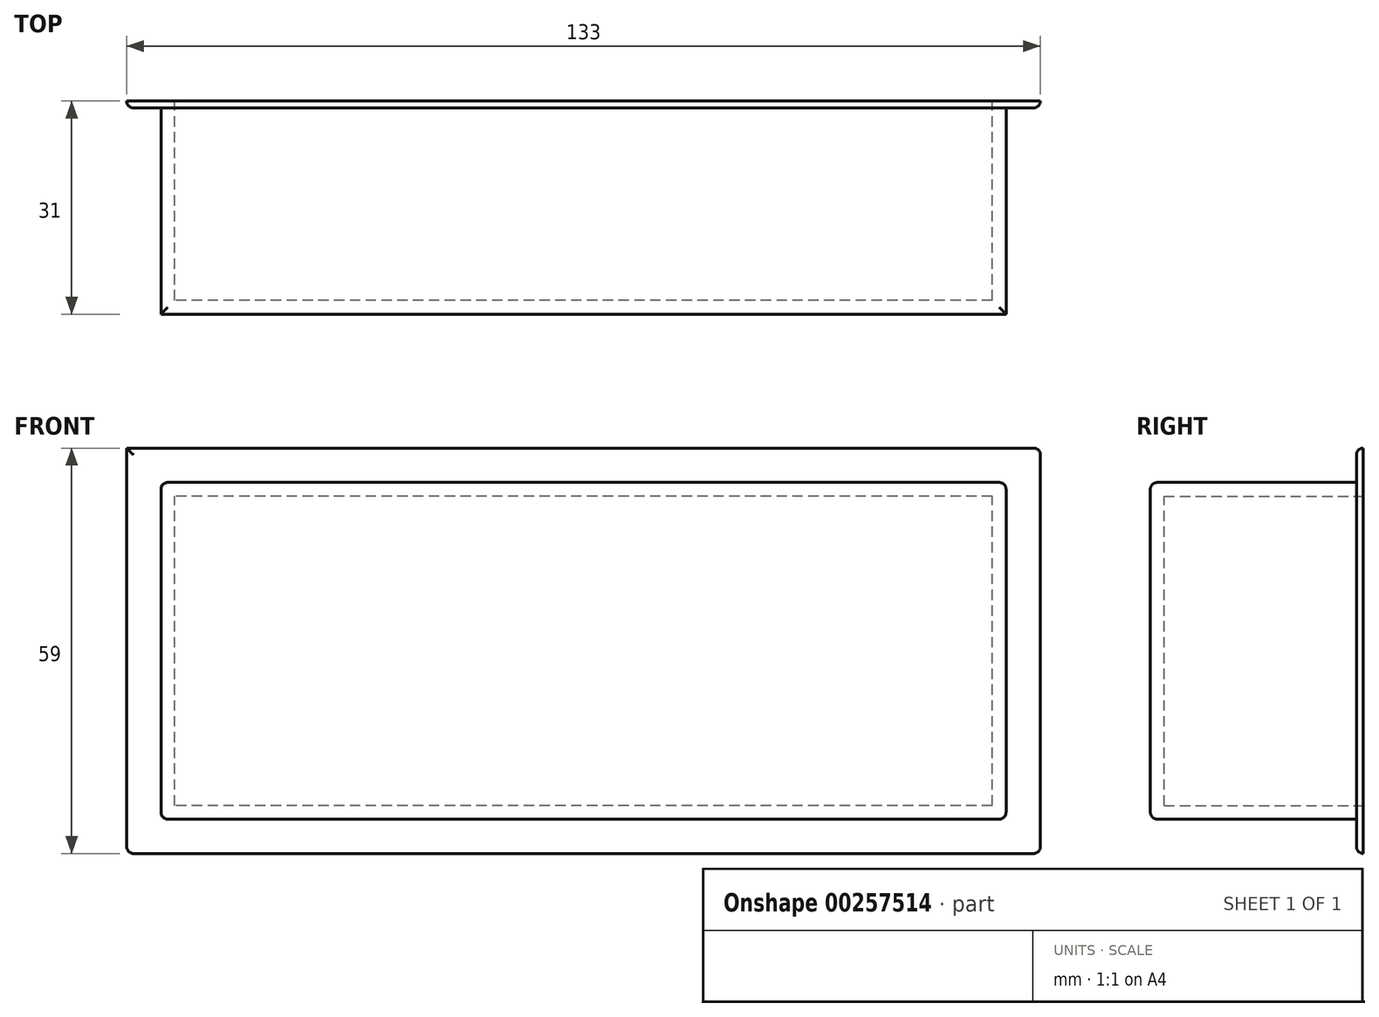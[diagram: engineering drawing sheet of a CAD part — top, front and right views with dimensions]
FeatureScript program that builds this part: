
annotation { "Feature Type Name" : "Feature", "Feature Type Description" : "" }
export const myFeature = defineFeature(function(context is Context, id is Id, definition is map)
    precondition{}
    {
        {
            var Q0;
            Q0=qCreatedBy(makeId("Front.planeOp"),FACE);
            cPlane(context, id + "F0", {"entities" : qUnion([Q0]), "cplaneType" : CPlaneType.OFFSET, "offset" : 15 * mm, "width" : 150 * mm, "height" : 150 * mm});
        }
        {
            var Q0;
            Q0=qCreatedBy(id+"F0.planeOp",FACE);
            var sketch = newSketch(context, id + "F1", { "sketchPlane" : qUnion([Q0])});
            skLineSegment(sketch, "E0.bottom", {"start": v(61.5, -24.5) * mm, "end": v(-61.5, -24.5) * mm});
            skLineSegment(sketch, "E0.top", {"start": v(61.5, 24.5) * mm, "end": v(-61.5, 24.5) * mm});
            skLineSegment(sketch, "E0.left", {"start": v(61.5, -24.5) * mm, "end": v(61.5, 24.5) * mm});
            skLineSegment(sketch, "E0.right", {"start": v(-61.5, -24.5) * mm, "end": v(-61.5, 24.5) * mm});
            skPoint(sketch, "E0.middle", {"position": v(0, 0) * mm});
            skLineSegment(sketch, "E1.bottom", {"start": v(59.5, -22.5) * mm, "end": v(-59.5, -22.5) * mm});
            skLineSegment(sketch, "E1.top", {"start": v(59.5, 22.5) * mm, "end": v(-59.5, 22.5) * mm});
            skLineSegment(sketch, "E1.left", {"start": v(59.5, -22.5) * mm, "end": v(59.5, 22.5) * mm});
            skLineSegment(sketch, "E1.right", {"start": v(-59.5, -22.5) * mm, "end": v(-59.5, 22.5) * mm});
            skLineSegment(sketch, "E2.top", {"start": v(61.5, 29.5) * mm, "end": v(-61.5, 29.5) * mm});
            skLineSegment(sketch, "E2.left", {"start": v(61.5, 24.5) * mm, "end": v(61.5, 29.5) * mm});
            skLineSegment(sketch, "E2.right", {"start": v(-61.5, 24.5) * mm, "end": v(-61.5, 29.5) * mm});
            skLineSegment(sketch, "E3.top", {"start": v(61.5, -29.5) * mm, "end": v(-61.5, -29.5) * mm});
            skLineSegment(sketch, "E3.left", {"start": v(61.5, -24.5) * mm, "end": v(61.5, -29.5) * mm});
            skLineSegment(sketch, "E3.right", {"start": v(-61.5, -24.5) * mm, "end": v(-61.5, -29.5) * mm});
            skLineSegment(sketch, "E4.bottom", {"start": v(-61.5, 29.5) * mm, "end": v(-66.5, 29.5) * mm});
            skLineSegment(sketch, "E4.top", {"start": v(-61.5, -29.5) * mm, "end": v(-66.5, -29.5) * mm});
            skLineSegment(sketch, "E4.left", {"start": v(-61.5, 29.5) * mm, "end": v(-61.5, -29.5) * mm});
            skLineSegment(sketch, "E4.right", {"start": v(-66.5, 29.5) * mm, "end": v(-66.5, -29.5) * mm});
            skLineSegment(sketch, "E5.bottom", {"start": v(61.5, 29.5) * mm, "end": v(66.5, 29.5) * mm});
            skLineSegment(sketch, "E5.top", {"start": v(61.5, -29.5) * mm, "end": v(66.5, -29.5) * mm});
            skLineSegment(sketch, "E5.left", {"start": v(61.5, 29.5) * mm, "end": v(61.5, -29.5) * mm});
            skLineSegment(sketch, "E5.right", {"start": v(66.5, 29.5) * mm, "end": v(66.5, -29.5) * mm});
            skSolve(sketch);
        }
        {
            var Q0;
            Q0=makeQuery(id+"F1.imprint","IMPRINT",FACE,{"disambiguationData":[TD([[makeQuery(id+"F1.imprint","IMPRINT",EDGE,{"derivedFrom":sQuery(id+"F1.wireOp",EDGE,"E1.bottom")}),1.0]])]});
            extrude(context, id + "F2", {"entities" : qUnion([Q0]), "depth" : 31 * mm});
        }
        {
            var Q0;
            {var subQ0=sQuery(id+"F1.wireOp",EDGE,"E0.top");Q0=makeQuery(id+"F1.imprint","IMPRINT",FACE,{"disambiguationData":[TD([[makeQuery(id+"F1.imprint","IMPRINT",EDGE,{"derivedFrom":subQ0}),-1.0]])]});}
            var Q1;
            {var subQ4=sQuery(id+"F1.wireOp",EDGE,"E4.bottom");Q1=makeQuery(id+"F1.imprint","IMPRINT",FACE,{"disambiguationData":[TD([[makeQuery(id+"F1.imprint","IMPRINT",EDGE,{"derivedFrom":subQ4}),1.0]])]});}
            var Q2;
            {var subQ0=sQuery(id+"F1.wireOp",EDGE,"E0.bottom");Q2=makeQuery(id+"F1.imprint","IMPRINT",FACE,{"disambiguationData":[TD([[makeQuery(id+"F1.imprint","IMPRINT",EDGE,{"derivedFrom":subQ0}),1.0]])]});}
            var Q3;
            {var subQ3=sQuery(id+"F1.wireOp",EDGE,"E5.bottom");Q3=makeQuery(id+"F1.imprint","IMPRINT",FACE,{"disambiguationData":[TD([[makeQuery(id+"F1.imprint","IMPRINT",EDGE,{"derivedFrom":subQ3}),-1.0]])]});}
            extrude(context, id + "F3", {"entities" : qUnion([Q0, Q1, Q2, Q3]), "operationType" : NewBodyOperationType.ADD, "depth" : 1 * mm});
        }
        {
            var Q0;
            Q0=makeQuery(id+"F1.imprint","IMPRINT",FACE,{"disambiguationData":[TD([[makeQuery(id+"F1.imprint","IMPRINT",EDGE,{"derivedFrom":sQuery(id+"F1.wireOp",EDGE,"E1.bottom")}),-1.0]])]});
            extrude(context, id + "F4", {"entities" : qUnion([Q0]), "operationType" : NewBodyOperationType.ADD, "depth" : 31 * mm});
        }
        {
            var Q0;
            Q0=makeQuery(id+"F1.imprint","IMPRINT",FACE,{"disambiguationData":[TD([[makeQuery(id+"F1.imprint","IMPRINT",EDGE,{"derivedFrom":sQuery(id+"F1.wireOp",EDGE,"E1.bottom")}),-1.0]])]});
            extrude(context, id + "F5", {"entities" : qUnion([Q0]), "operationType" : NewBodyOperationType.REMOVE, "depth" : 29 * mm});
        }
        {
            var Q0;
            Q0=makeQuery(id+"F2.opExtrude","SWEPT_EDGE",EDGE,{"disambiguationData":[OSD([sQuery(id+"F1.wireOp",EDGE,"E0.top"),sQuery(id+"F1.wireOp",EDGE,"E5.left")])]});
            var Q1;
            Q1=makeQuery(id+"F2.opExtrude","SWEPT_EDGE",EDGE,{"disambiguationData":[OSD([sQuery(id+"F1.wireOp",EDGE,"E0.bottom"),sQuery(id+"F1.wireOp",EDGE,"E5.left")])]});
            var Q2;
            Q2=makeQuery(id+"F2.opExtrude","SWEPT_FACE",FACE,{"disambiguationData":[OSD([sQuery(id+"F1.wireOp",EDGE,"E5.left")])]});
            var Q3;
            Q3=makeQuery(id+"F2.opExtrude","CAP_EDGE",EDGE,{"disambiguationData":[OSD([sQuery(id+"F1.wireOp",EDGE,"E0.bottom")])],"isStart":false});
            var Q4;
            Q4=makeQuery(id+"F2.opExtrude","CAP_EDGE",EDGE,{"disambiguationData":[OSD([sQuery(id+"F1.wireOp",EDGE,"E0.top")])],"isStart":false});
            var Q5;
            Q5=makeQuery(id+"F2.opExtrude","SWEPT_EDGE",EDGE,{"disambiguationData":[OSD([sQuery(id+"F1.wireOp",EDGE,"E0.bottom"),sQuery(id+"F1.wireOp",EDGE,"E4.left")])]});
            var Q6;
            Q6=makeQuery(id+"F2.opExtrude","SWEPT_EDGE",EDGE,{"disambiguationData":[OSD([sQuery(id+"F1.wireOp",EDGE,"E0.top"),sQuery(id+"F1.wireOp",EDGE,"E4.left")])]});
            var Q7;
            Q7=makeQuery(id+"F2.opExtrude","SWEPT_FACE",FACE,{"disambiguationData":[OSD([sQuery(id+"F1.wireOp",EDGE,"E4.left")])]});
            var Q8;
            Q8=makeQuery(id+"F3.opExtrude","CAP_EDGE",EDGE,{"disambiguationData":[OSD([sQuery(id+"F1.wireOp",EDGE,"E3.top"),sQuery(id+"F1.wireOp",EDGE,"E4.top"),sQuery(id+"F1.wireOp",EDGE,"E5.top")])],"isStart":false});
            var Q9;
            Q9=makeQuery(id+"F3.opExtrude","CAP_EDGE",EDGE,{"disambiguationData":[OSD([sQuery(id+"F1.wireOp",EDGE,"E4.right")])],"isStart":false});
            var Q10;
            Q10=makeQuery(id+"F3.opExtrude","CAP_EDGE",EDGE,{"disambiguationData":[OSD([sQuery(id+"F1.wireOp",EDGE,"E2.top"),sQuery(id+"F1.wireOp",EDGE,"E4.bottom"),sQuery(id+"F1.wireOp",EDGE,"E5.bottom")])],"isStart":false});
            var Q11;
            Q11=makeQuery(id+"F3.opExtrude","CAP_EDGE",EDGE,{"disambiguationData":[OSD([sQuery(id+"F1.wireOp",EDGE,"E5.right")])],"isStart":false});
            fillet(context, id + "F6", {"entities" : qUnion([Q0, Q1, Q2, Q3, Q4, Q5, Q6, Q7, Q8, Q9, Q10, Q11]), "radius" : 1 * mm, "tangentPropagation" : true, "allowEdgeOverflow" : false});
        }
        {
            var Q0;
            Q0=makeQuery(id+"F3.opExtrude","SWEPT_EDGE",EDGE,{"disambiguationData":[OSD([sQuery(id+"F1.wireOp",EDGE,"E4.bottom"),sQuery(id+"F1.wireOp",EDGE,"E4.right")])]});
            var Q1;
            Q1=makeQuery(id+"F6.opFillet","BLEND_EDGE",EDGE,{"blendedFrom":[makeQuery(id+"F3.opExtrude","CAP_EDGE",EDGE,{"disambiguationData":[OSD([sQuery(id+"F1.wireOp",EDGE,"E3.top"),sQuery(id+"F1.wireOp",EDGE,"E4.top"),sQuery(id+"F1.wireOp",EDGE,"E5.top")])],"isStart":false}),makeQuery(id+"F3.opExtrude","CAP_EDGE",EDGE,{"disambiguationData":[OSD([sQuery(id+"F1.wireOp",EDGE,"E4.right")])],"isStart":false})],"blendedInto":[]});
            var Q2;
            Q2=makeQuery(id+"F6.opFillet","BLEND_EDGE",EDGE,{"blendedFrom":[makeQuery(id+"F3.opExtrude","CAP_EDGE",EDGE,{"disambiguationData":[OSD([sQuery(id+"F1.wireOp",EDGE,"E3.top"),sQuery(id+"F1.wireOp",EDGE,"E4.top"),sQuery(id+"F1.wireOp",EDGE,"E5.top")])],"isStart":false}),makeQuery(id+"F3.opExtrude","CAP_EDGE",EDGE,{"disambiguationData":[OSD([sQuery(id+"F1.wireOp",EDGE,"E5.right")])],"isStart":false})],"blendedInto":[]});
            var Q3;
            Q3=makeQuery(id+"F6.opFillet","BLEND_EDGE",EDGE,{"blendedFrom":[makeQuery(id+"F3.opExtrude","CAP_EDGE",EDGE,{"disambiguationData":[OSD([sQuery(id+"F1.wireOp",EDGE,"E2.top"),sQuery(id+"F1.wireOp",EDGE,"E4.bottom"),sQuery(id+"F1.wireOp",EDGE,"E5.bottom")])],"isStart":false}),makeQuery(id+"F3.opExtrude","CAP_EDGE",EDGE,{"disambiguationData":[OSD([sQuery(id+"F1.wireOp",EDGE,"E5.right")])],"isStart":false})],"blendedInto":[]});
            fillet(context, id + "F7", {"entities" : qUnion([Q0, Q1, Q2, Q3]), "radius" : 1 * mm, "tangentPropagation" : true, "allowEdgeOverflow" : false});
        }
    });
